# Revit family: Table-Teknion-CWRT_Reception_With_Transaction-R2016
name_source: partatom
category: Furniture
revit_build: Autodesk Revit 2018 (Build: 20190510_1515(x64)
units: mm (PartAtom-declared; Revit-internal decimal feet)

## family parameters
Always vertical = Yes
Cut with Voids When Loaded = No
OmniClass Number = 23.40.20.00
OmniClass Title = General Furniture and Specialties
Room Calculation Point = No
Shared = Yes
Work Plane-Based = No

## types (3) — shared parameters
Assembly Code = E2020200
Manufacturer = Teknion
Manufacturer Fax = 416.661.4586
Part Number = CWRT
Product Documentation Link = https://assets.teknion.com
Product Line = Reception
Product Page URL = https://www.teknion.com
Series = Custom Wood
Sustainability Data = https://www.teknion.com
URL = www.teknion.com
Unit Weight URL = http://www.teknion.com
Warranty = http://www.teknion.com

## per-type parameters (varying)
| type | Center | Closed | Description | Edge offset | LeftorRight | Model | Open |
| Left/Right Transaction Counter with Open Waterfall Edge | No | No | Teknion Recption with Transaction, Open Waterfall Edge, Left/Right Transaction Counter | 3 " | Yes | CWRT__O_ | Yes |
| Left/Right Transaction Counter with Closed Waterfall Edge | No | Yes | Teknion Recption with Transaction, Closed Waterfall Edge, Left/Right Transaction Counter | 3 " | Yes | CWRT__C_ | No |
| Center Transaction Counter with Closed Waterfall Edge | Yes | Yes | Teknion Recption with Transaction, Closed Waterfall Edge, Center Transaction Counter | 0 " | No | CWRT__CC | No |

## geometry (parser evidence)
native form markers: Sweep x5
no freeform markers — native parametric forms only
